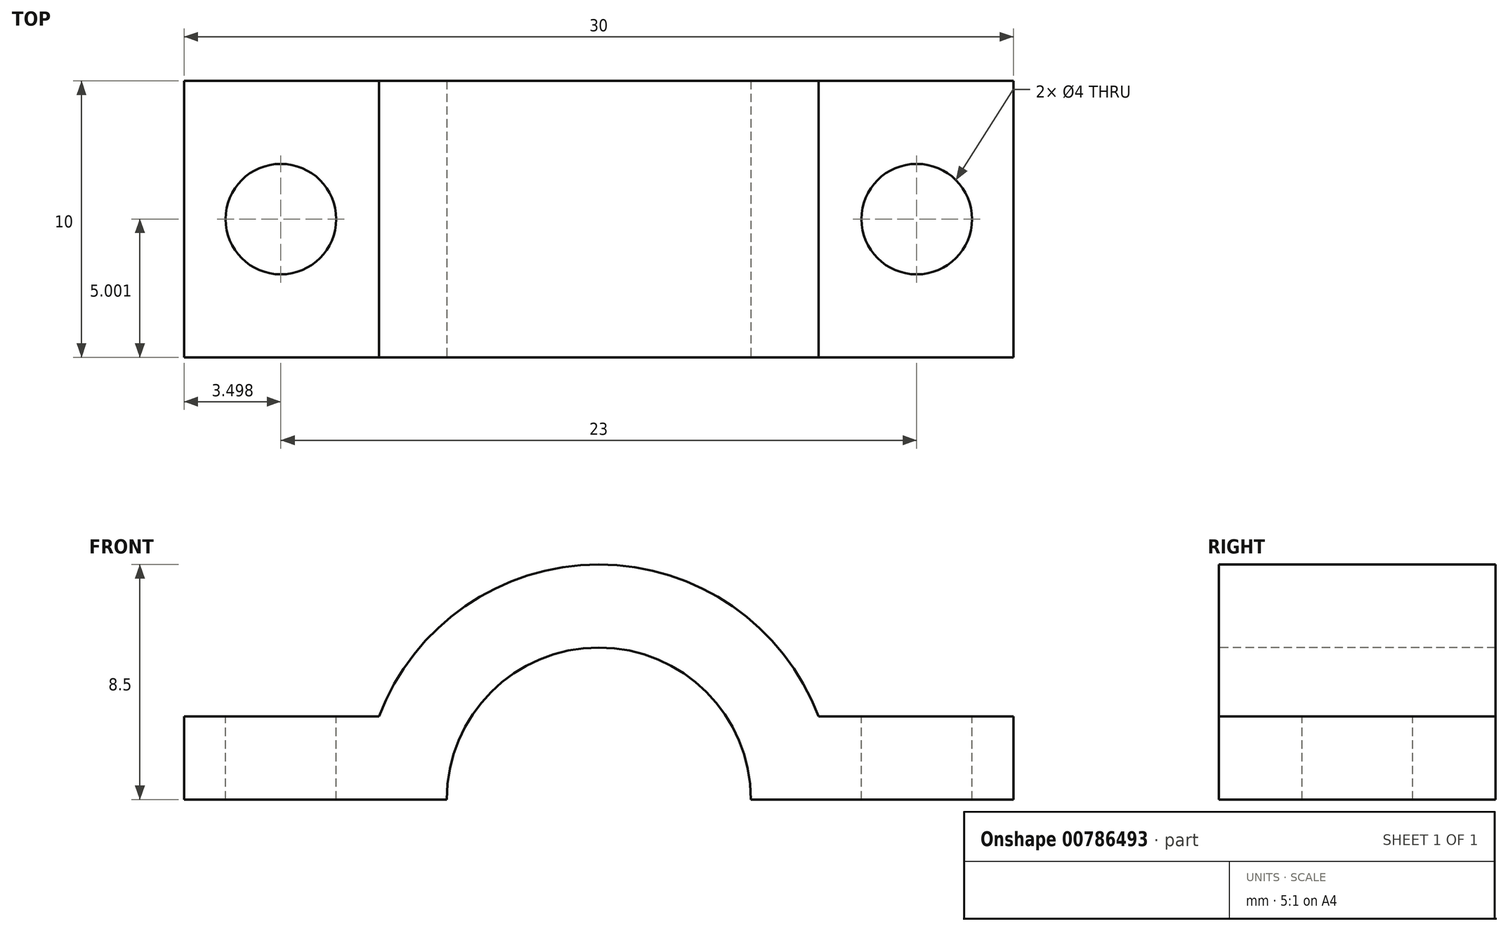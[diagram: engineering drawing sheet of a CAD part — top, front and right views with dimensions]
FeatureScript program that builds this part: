
annotation { "Feature Type Name" : "Feature", "Feature Type Description" : "" }
export const myFeature = defineFeature(function(context is Context, id is Id, definition is map)
    precondition{}
    {
        {
            var Q0;
            Q0=qCreatedBy(makeId("Top.planeOp"),FACE);
            var sketch = newSketch(context, id + "F0", { "sketchPlane" : qUnion([Q0])});
            skLineSegment(sketch, "E0.bottom", {"start": v(-9.15, 6.41) * mm, "end": v(20.85, 6.41) * mm});
            skLineSegment(sketch, "E0.top", {"start": v(-9.15, -3.59) * mm, "end": v(20.85, -3.59) * mm});
            skLineSegment(sketch, "E0.left", {"start": v(-9.15, 6.41) * mm, "end": v(-9.15, -3.59) * mm});
            skLineSegment(sketch, "E0.right", {"start": v(20.85, 6.41) * mm, "end": v(20.85, -3.59) * mm});
            skSolve(sketch);
        }
        {
            var Q0;
            Q0=makeQuery(id+"F0.imprint","IMPRINT",FACE,{"disambiguationData":[TD([[makeQuery(id+"F0.imprint","IMPRINT",EDGE,{"derivedFrom":sQuery(id+"F0.wireOp",EDGE,"E0.bottom")}),-1.0]])]});
            extrude(context, id + "F1", {"entities" : qUnion([Q0]), "depth" : 17 * mm, "offsetDistance" : 25 * mm});
        }
        {
            var Q0;
            Q0=makeQuery(id+"F1.opExtrude","SWEPT_FACE",FACE,{"disambiguationData":[OSD([sQuery(id+"F0.wireOp",EDGE,"E0.top")])]});
            var sketch = newSketch(context, id + "F2", { "sketchPlane" : qUnion([Q0])});
            skCircle(sketch, "E1", {"center": v(5.85, 0) * mm, "radius": 5.5 * mm});
            skCircle(sketch, "E2", {"center": v(5.85, 0) * mm, "radius": 8.5 * mm});
            skLineSegment(sketch, "E3", {"start": v(-9.15, 3) * mm, "end": v(-2.1, 3) * mm});
            skLineSegment(sketch, "E4", {"start": v(13.8, 3) * mm, "end": v(20.85, 3) * mm});
            skSolve(sketch);
        }
        {
            var Q0;
            {var subQ1=sQuery(id+"F2.wireOp",EDGE,"E3");Q0=makeQuery(id+"F2.imprint","IMPRINT",FACE,{"disambiguationData":[TD([[makeQuery(id+"F2.imprint","IMPRINT",EDGE,{"derivedFrom":subQ1}),1.0]])]});}
            var Q1;
            {var subQ0=sQuery(id+"F2.wireOp",EDGE,"E1");var subQ1=makeQuery(id+"F1.opExtrude","CAP_EDGE",EDGE,{"disambiguationData":[OSD([sQuery(id+"F0.wireOp",EDGE,"E0.top")])],"isStart":true});var subQ2=makeQuery(id+"F2.imprint","INTERSECT",VERTEX,{"disambiguationData":[OD(0.0)],"derivedFrom":[subQ1,subQ0]});Q1=makeQuery(id+"F2.imprint","IMPRINT",FACE,{"disambiguationData":[TD([[makeQuery(id+"F2.imprint","IMPRINT",EDGE,{"disambiguationData":[TD([[subQ2,-1.0]])],"derivedFrom":subQ0}),1.0]])]});}
            extrude(context, id + "F3", {"entities" : qUnion([Q0, Q1]), "operationType" : NewBodyOperationType.REMOVE, "oppositeDirection" : true, "depth" : 25 * mm, "offsetDistance" : 25 * mm});
        }
        {
            var Q0;
            Q0=makeQuery(id+"F3.boolean.opBoolean","COPY",FACE,{"derivedFrom":makeQuery(id+"F3.opExtrude","SWEPT_FACE",FACE,{"disambiguationData":[OSD([sQuery(id+"F2.wireOp",EDGE,"E3")])]})});
            var sketch = newSketch(context, id + "F4", { "sketchPlane" : qUnion([Q0])});
            skCircle(sketch, "E5", {"center": v(-5.65, 1.41) * mm, "radius": 2 * mm});
            skCircle(sketch, "E6", {"center": v(17.35, 1.41) * mm, "radius": 2 * mm});
            skLineSegment(sketch, "E7", {"start": v(-9.15, -3.59) * mm, "end": v(-2.1, -3.59) * mm});
            skSolve(sketch);
        }
        {
            var Q0;
            Q0=qSketchRegion(id+"F4",true);
            extrude(context, id + "F5", {"entities" : qUnion([Q0]), "operationType" : NewBodyOperationType.REMOVE, "oppositeDirection" : true, "depth" : 25 * mm, "offsetDistance" : 25 * mm});
        }
    });
